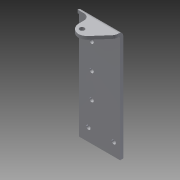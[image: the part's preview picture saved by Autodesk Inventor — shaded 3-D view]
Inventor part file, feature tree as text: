
AUTODESK INVENTOR PART (.ipt)
format: ipt  version: 2014 (Build 180170000, 170)  size: 204,800 bytes
history: native  units: in
note: dims shown in document units (in); Inventor stores cm internally (conversion verified against a paired STEP export)
features: other x5, sheet_metal_op x4, sketch x2, fillet x1
ambient origin geometry x8: Origin, YZ Plane, XZ Plane, XY Plane, X Axis, Y Axis, Z Axis, Center Point
bodies: Solid1 (feature_tree)
feature tree (12):
  sheet_metal_op  "Face1"
  sheet_metal_op  "Flange1"
  fillet  "Fillet3"  Radius=1.625in
  sketch  "Sketch1"  dims[d1=4.1875in]
  other  "Plate1"
  sketch  "Sketch2"  dims[d2=0.163in d4=0.7874in d6=1.0in d7=0.3937in d9=1.0in d11=0.125in d12=0.125in d13=0.0625in d14=0.25in d15=0.125in d16=1.0in d17=90.0deg d18=0.05in d19=0.5in d20=0.125in d21=0.125in d22=0.5in d28=0.187in d29=0.25in d34=0.75in d36=0.25in d38=0.5in d39=1.5in d40=1.1811in d42=1.0in d43=0.3937in d45=1.0in d47=0.125in d48=0.25in d49=0.25in d50=0.375in d51=0.125in d52=0.0in d53=0.25in d3=0.0in]
  other  "Plate2"
  sheet_metal_op  "Bend1"
  sheet_metal_op  "Corner1"
  other  "Cut3"
  other  "Definition1"
  other  "Cut1"
